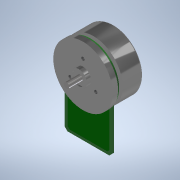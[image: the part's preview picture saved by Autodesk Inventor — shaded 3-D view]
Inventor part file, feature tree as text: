
AUTODESK INVENTOR PART (.ipt)
format: ipt  version: 2020.2 (Build 242310000, 310)  size: 229,888 bytes
history: native  units: mm
features: sketch x5, extrude x4, projected_geometry x2, other x1, revolve x1, fillet x1, hole x1, pattern_circular x1, chamfer x1
ambient origin geometry x8: Origin, YZ Plane, XZ Plane, XY Plane, X Axis, Y Axis, Z Axis, Center Point
bodies: Volumenkörper1 (feature_tree)
feature tree (17):
  other  "MaxonEC45-50W-MILE"
  revolve  "Umdrehung1"
  fillet  "Rundung1"  Radius=44.0mm
  extrude  "Extrusion1"  Depth=1.6mm
  hole  "Bohrung1"  [1 undecoded]
  pattern_circular  "Runde Anordnung1"  [2 undecoded]
  extrude  "Extrusion2"  Depth=0.01mm
  chamfer  "Fase1"  Distance=42.4mm
  extrude  "Extrusion3"  Depth=0.01mm
  extrude  "Extrusion4"  TaperAngle=90.0deg  [1 undecoded]
  sketch  "Skizze1"  dims[d1=4.0mm d2=1.6mm]
  sketch  "Skizze3"  dims[d3=2.1mm d4=22.6mm]
  sketch  "Skizze4"  dims[d5=43.4mm]
  sketch  "Sketch5"  dims[d6=12.0mm]
  projected_geometry  "Projected Loop1"
  sketch  "Sketch6"  dims[d7=4.0mm d8=3.2mm d9=20.2mm d10=42.4mm d11=36.5mm d12=90.0deg d13=1.0mm d14=1.0mm d15=1.0mm d16=0.0mm d17=11.0mm d18=2.459mm d19=6.0mm d20=4.0mm d21=2.0mm d22=90.0deg d23=3.9mm d24=20.594885mm d25=30.0mm d26=360.0deg d28=35.0mm d29=45.3mm d30=1.6mm d31=0.0mm d32=2.0mm d33=2.0mm d34=45.0deg d35=2.0mm d36=30.0mm d37=2.0mm d38=135.0deg d39=28.0mm d40=135.0deg d41=2.0mm d42=135.0deg d43=0.01mm d44=0.0mm d45=8.0mm d46=0.0mm]
  projected_geometry  "Projected Loop2"
note: 4 required parameter values undecoded (feature->parameter linkage not recoverable at this tier; creation-order binding heuristic only, values carry confidence <= 0.55)
